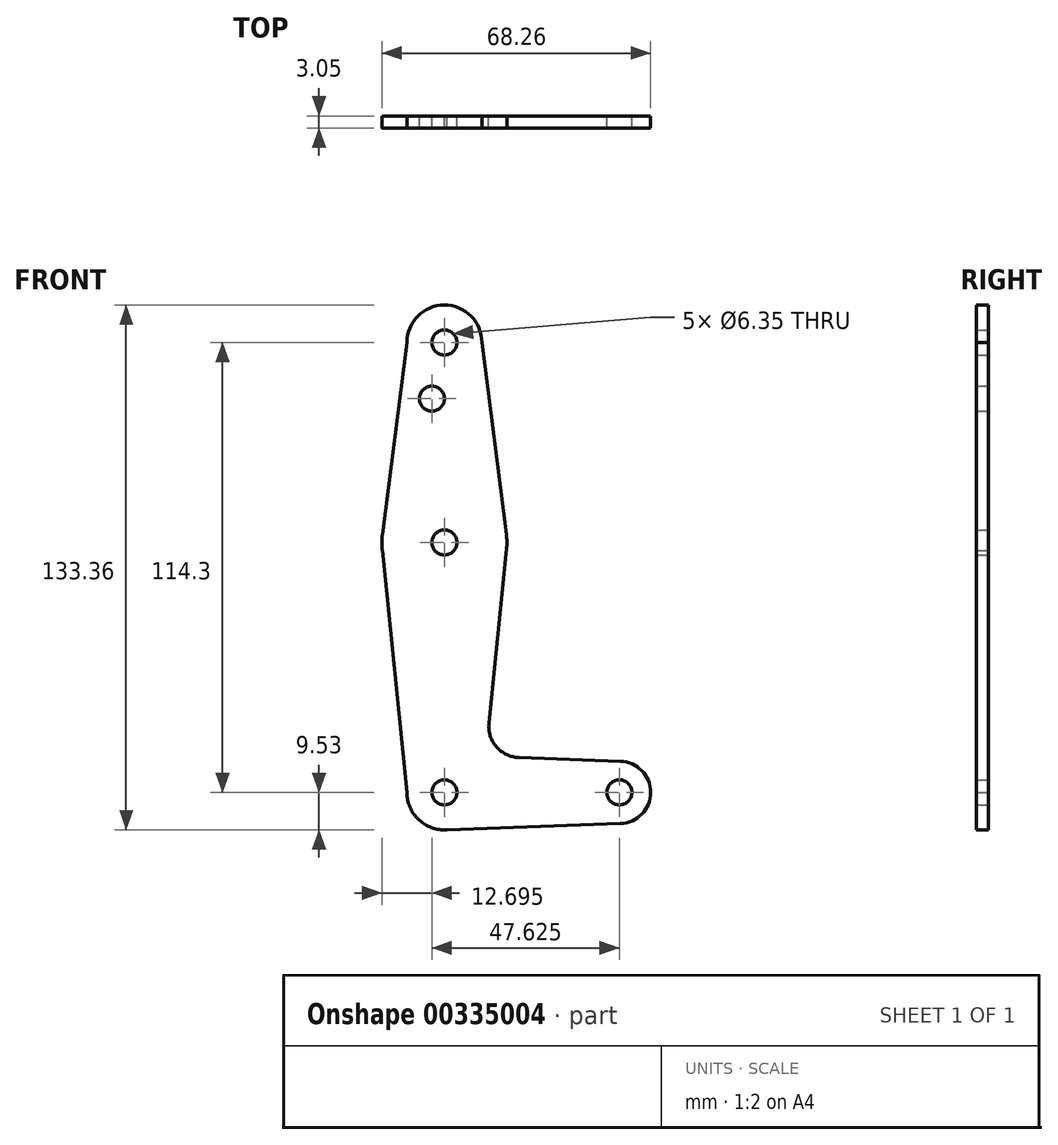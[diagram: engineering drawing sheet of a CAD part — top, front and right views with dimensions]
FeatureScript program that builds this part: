
annotation { "Feature Type Name" : "Feature", "Feature Type Description" : "" }
export const myFeature = defineFeature(function(context is Context, id is Id, definition is map)
    precondition{}
    {
        {
            var Q0;
            Q0=qCreatedBy(makeId("Front.planeOp"),FACE);
            var sketch = newSketch(context, id + "F0", { "sketchPlane" : qUnion([Q0])});
            skLineSegment(sketch, "E0", {"start": v(0, 0) * mm, "end": v(0, 114.3) * mm});
            skLineSegment(sketch, "E1", {"start": v(0, 0) * mm, "end": v(44.45, 0) * mm});
            skCircle(sketch, "E2", {"center": v(0, 114.3) * mm, "radius": 9.53 * mm});
            skCircle(sketch, "E3", {"center": v(0, 0) * mm, "radius": 9.53 * mm});
            skCircle(sketch, "E4", {"center": v(0, 63.5) * mm, "radius": 15.88 * mm});
            skCircle(sketch, "E5", {"center": v(44.45, 0) * mm, "radius": 7.94 * mm});
            skLineSegment(sketch, "E6", {"start": v(18.93, 8.85) * mm, "end": v(44.73, 7.93) * mm});
            skLineSegment(sketch, "E7", {"start": v(0, -9.53) * mm, "end": v(44.73, -7.93) * mm});
            skLineSegment(sketch, "E8", {"start": v(-9.53, 114.3) * mm, "end": v(-15.75, 65.5) * mm});
            skLineSegment(sketch, "E9", {"start": v(9.52, 114.3) * mm, "end": v(15.75, 65.5) * mm});
            skLineSegment(sketch, "E10", {"start": v(-15.75, 61.5) * mm, "end": v(-9.53, 0) * mm});
            skLineSegment(sketch, "E11", {"start": v(11.3, 17.6) * mm, "end": v(15.8, 61.9) * mm});
            skCircle(sketch, "E12", {"center": v(0, 114.3) * mm, "radius": 3.18 * mm});
            skCircle(sketch, "E13", {"center": v(0, 63.5) * mm, "radius": 3.17 * mm});
            skCircle(sketch, "E14", {"center": v(0, 0) * mm, "radius": 3.18 * mm});
            skCircle(sketch, "E15", {"center": v(44.45, 0) * mm, "radius": 3.18 * mm});
            skCircle(sketch, "E16", {"center": v(-3.17, 100.03) * mm, "radius": 3.18 * mm});
            skArc(sketch, "E17.filletArc", {"start": v(11.3, 17.6) * mm, "mid": v(13.22, 11.57) * mm, "end": v(18.93, 8.85) * mm});
            skSolve(sketch);
        }
        {
            var Q0;
            Q0 = qSketchRegion(id + "F0", true);
            var Q1;
            {var subQ0=sQuery(id+"F0.wireOp",EDGE,"E14");var subQ1=sQuery(id+"F0.wireOp",EDGE,"E0");var subQ2=makeQuery(id+"F0.imprint","INTERSECT",VERTEX,{"derivedFrom":[subQ1,subQ0]});Q1=makeQuery(id+"F0.imprint","IMPRINT",FACE,{"disambiguationData":[TD([[makeQuery(id+"F0.imprint","IMPRINT",EDGE,{"disambiguationData":[TD([[subQ2,-1.0]])],"derivedFrom":subQ1}),-1.0]])]});}
            extrude(context, id + "F1", {"entities" : qUnion([Q0, Q1]), "depth" : 3.05 * mm});
        }
    });
